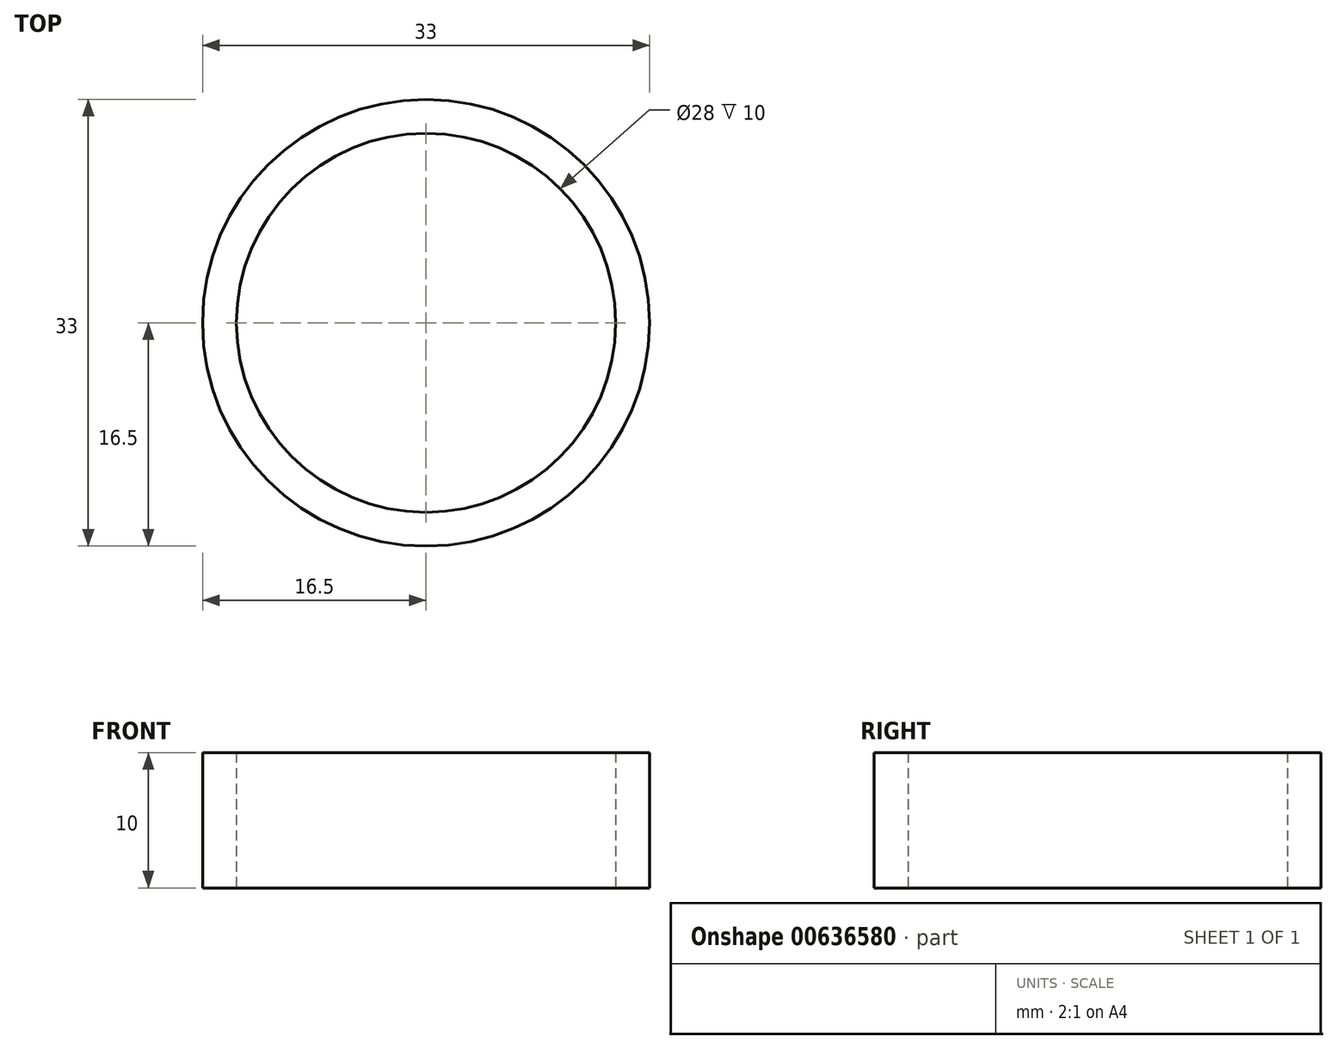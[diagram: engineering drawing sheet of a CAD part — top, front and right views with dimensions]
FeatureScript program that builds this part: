
annotation { "Feature Type Name" : "Feature", "Feature Type Description" : "" }
export const myFeature = defineFeature(function(context is Context, id is Id, definition is map)
    precondition{}
    {
        {
            var Q0;
            Q0=qCreatedBy(makeId("Top.planeOp"),FACE);
            var sketch = newSketch(context, id + "F0", { "sketchPlane" : qUnion([Q0])});
            skCircle(sketch, "E0", {"center": v(0, 0) * mm, "radius": 16.5 * mm});
            skCircle(sketch, "E1", {"center": v(0, 0) * mm, "radius": 14 * mm});
            skSolve(sketch);
        }
        {
            var Q0;
            Q0=makeQuery(id+"F0.imprint","IMPRINT",FACE,{"disambiguationData":[TD([[makeQuery(id+"F0.imprint","IMPRINT",EDGE,{"derivedFrom":sQuery(id+"F0.wireOp",EDGE,"E0")}),1.0]])]});
            extrude(context, id + "F1", {"entities" : qUnion([Q0]), "depth" : 10 * mm, "offsetDistance" : 25 * mm});
        }
    });
